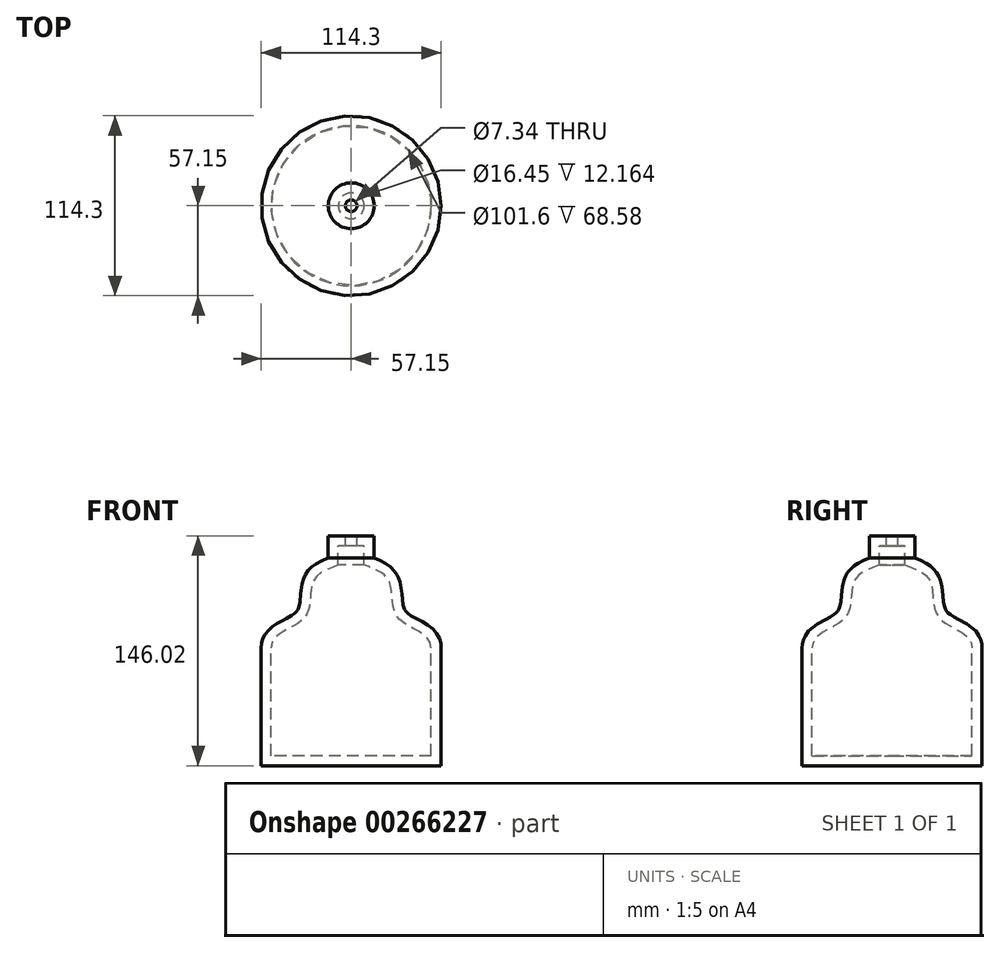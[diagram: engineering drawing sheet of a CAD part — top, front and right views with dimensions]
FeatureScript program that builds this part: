
annotation { "Feature Type Name" : "Feature", "Feature Type Description" : "" }
export const myFeature = defineFeature(function(context is Context, id is Id, definition is map)
    precondition{}
    {
        {
            var Q0;
            Q0=qCreatedBy(makeId("Front.planeOp"),FACE);
            var sketch = newSketch(context, id + "F0", { "sketchPlane" : qUnion([Q0])});
            skLineSegment(sketch, "E0", {"start": v(0, -68.58) * mm, "end": v(50.8, -68.58) * mm});
            skLineSegment(sketch, "E1", {"start": v(50.8, -68.58) * mm, "end": v(50.8, 0) * mm});
            skFitSpline(sketch, "E2", {"points": [v(50.8, 0) * mm, v(29.96, 18.8) * mm, v(24.08, 42.3) * mm, v(8.22, 52.57) * mm], "startDerivative": vector(0, 83.6) * mm, "endDerivative": vector(-64.5, 24.57) * mm});
            skLineSegment(sketch, "E3", {"start": v(8.22, 52.57) * mm, "end": v(8.22, 64.74) * mm});
            skLineSegment(sketch, "E4", {"start": v(8.22, 64.74) * mm, "end": v(0, 64.74) * mm});
            skLineSegment(sketch, "E5.0", {"start": v(14.57, 71.09) * mm, "end": v(3.67, 71.09) * mm});
            skLineSegment(sketch, "E5.1", {"start": v(0, -74.93) * mm, "end": v(57.15, -74.93) * mm});
            skLineSegment(sketch, "E5.2", {"start": v(57.15, -74.93) * mm, "end": v(57.15, 0) * mm});
            skFitSpline(sketch, "E5.3", {"points": [v(57.15, 0) * mm, v(57.15, 0.7) * mm, v(57.06, 2.1) * mm, v(56.65, 4.13) * mm, v(55.99, 6.03) * mm, v(55.11, 7.77) * mm, v(54.08, 9.33) * mm, v(52.55, 11.17) * mm, v(50.45, 13.07) * mm, v(47.85, 14.9) * mm, v(45.25, 16.43) * mm, v(42.73, 17.78) * mm, v(40.37, 19.02) * mm, v(38.62, 20) * mm, v(37.4, 20.77) * mm, v(36.58, 21.32) * mm, v(35.89, 21.85) * mm, v(35.32, 22.35) * mm, v(34.95, 22.73) * mm, v(34.72, 23) * mm, v(34.55, 23.22) * mm, v(34.4, 23.44) * mm, v(34.19, 23.76) * mm, v(33.85, 24.38) * mm, v(33.41, 25.45) * mm, v(32.98, 27.05) * mm, v(32.65, 28.93) * mm, v(32.41, 31.04) * mm, v(32.21, 33.33) * mm, v(32, 35.76) * mm, v(31.71, 38.3) * mm, v(31.32, 40.5) * mm, v(30.85, 42.32) * mm, v(30.47, 43.47) * mm, v(30.1, 44.4) * mm, v(29.79, 45.1) * mm, v(29.44, 45.78) * mm, v(28.95, 46.67) * mm, v(28.28, 47.71) * mm, v(27.09, 49.25) * mm, v(25.44, 50.93) * mm, v(23.33, 52.58) * mm, v(21.14, 53.95) * mm, v(18.94, 55.1) * mm, v(16.74, 56.08) * mm, v(13.85, 57.25) * mm, v(11.78, 58.01) * mm, v(10.48, 58.5) * mm]});
            skLineSegment(sketch, "E5.4", {"start": v(14.57, 56.95) * mm, "end": v(14.57, 71.09) * mm});
            skLineSegment(sketch, "E6", {"start": v(3.67, 71.09) * mm, "end": v(0, 64.74) * mm});
            skLineSegment(sketch, "E7", {"start": v(0, -68.58) * mm, "end": v(0, -74.93) * mm});
            skLineSegment(sketch, "E8", {"start": v(3.67, 71.09) * mm, "end": v(3.67, 64.74) * mm});
            skSolve(sketch);
        }
        {
            var Q0;
            Q0=makeQuery(id+"F0.imprint","IMPRINT",FACE,{"disambiguationData":[TD([[makeQuery(id+"F0.imprint","IMPRINT",EDGE,{"derivedFrom":sQuery(id+"F0.wireOp",EDGE,"E0")}),-1.0]])]});
            var Q1;
            Q1=sQuery(id+"F0.wireOp",EDGE,"E7");
            revolve(context, id + "F1", {"entities" : qUnion([Q0]), "axis" : qUnion([Q1]), "revolveType" : RevolveType.FULL});
        }
    });
